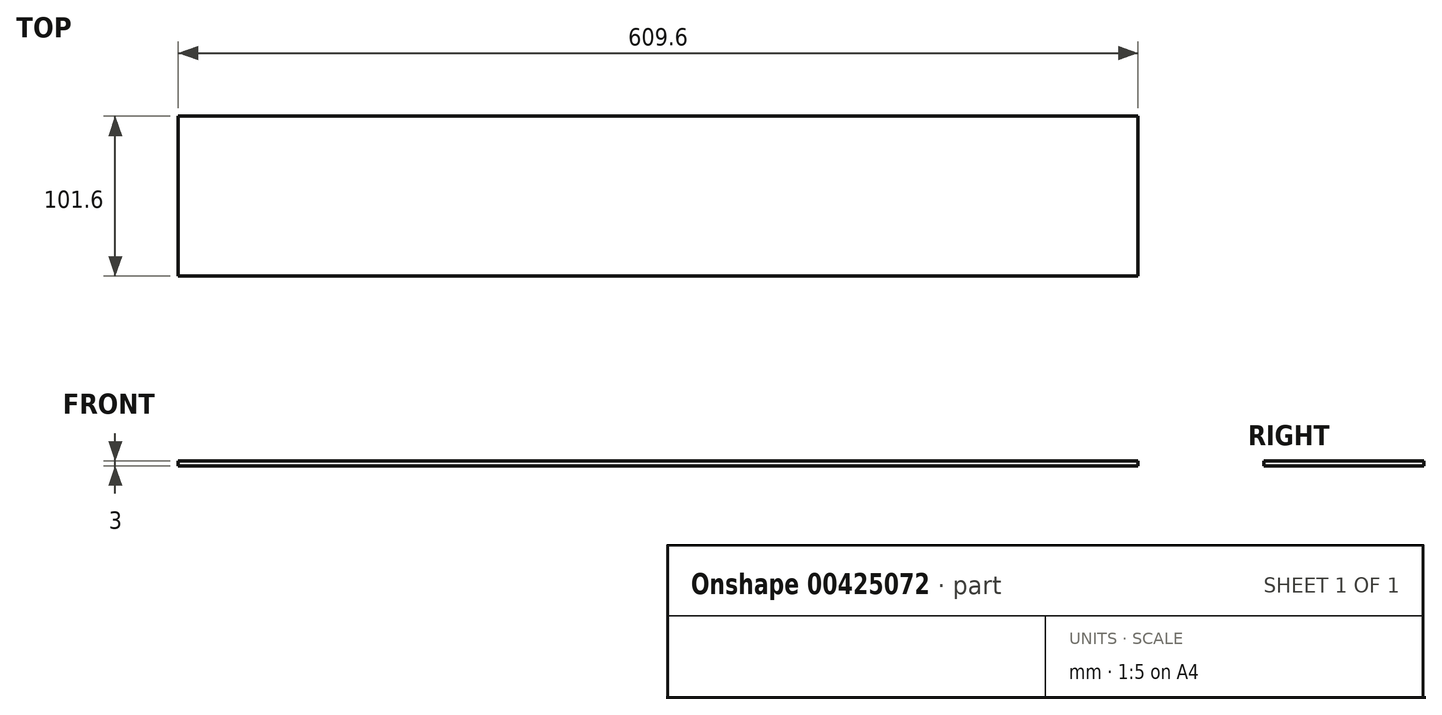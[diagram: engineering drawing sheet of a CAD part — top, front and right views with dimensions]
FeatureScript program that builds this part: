
annotation { "Feature Type Name" : "Feature", "Feature Type Description" : "" }
export const myFeature = defineFeature(function(context is Context, id is Id, definition is map)
    precondition{}
    {
        {
            var Q0;
            Q0=qCreatedBy(makeId("Top.planeOp"),FACE);
            var sketch = newSketch(context, id + "F0", { "sketchPlane" : qUnion([Q0])});
            skLineSegment(sketch, "E0.bottom", {"start": v(-347.64, -143.18) * mm, "end": v(261.96, -143.18) * mm});
            skLineSegment(sketch, "E0.top", {"start": v(-347.64, -244.78) * mm, "end": v(261.96, -244.78) * mm});
            skLineSegment(sketch, "E0.left", {"start": v(-347.64, -143.18) * mm, "end": v(-347.64, -244.78) * mm});
            skLineSegment(sketch, "E0.right", {"start": v(261.96, -143.18) * mm, "end": v(261.96, -244.78) * mm});
            skSolve(sketch);
        }
        {
            var Q0;
            Q0=makeQuery(id+"F0.imprint","IMPRINT",FACE,{"disambiguationData":[TD([[makeQuery(id+"F0.imprint","IMPRINT",EDGE,{"derivedFrom":sQuery(id+"F0.wireOp",EDGE,"E0.bottom")}),-1.0]])]});
            extrude(context, id + "F1", {"entities" : qUnion([Q0]), "depth" : 3 * mm});
        }
    });
